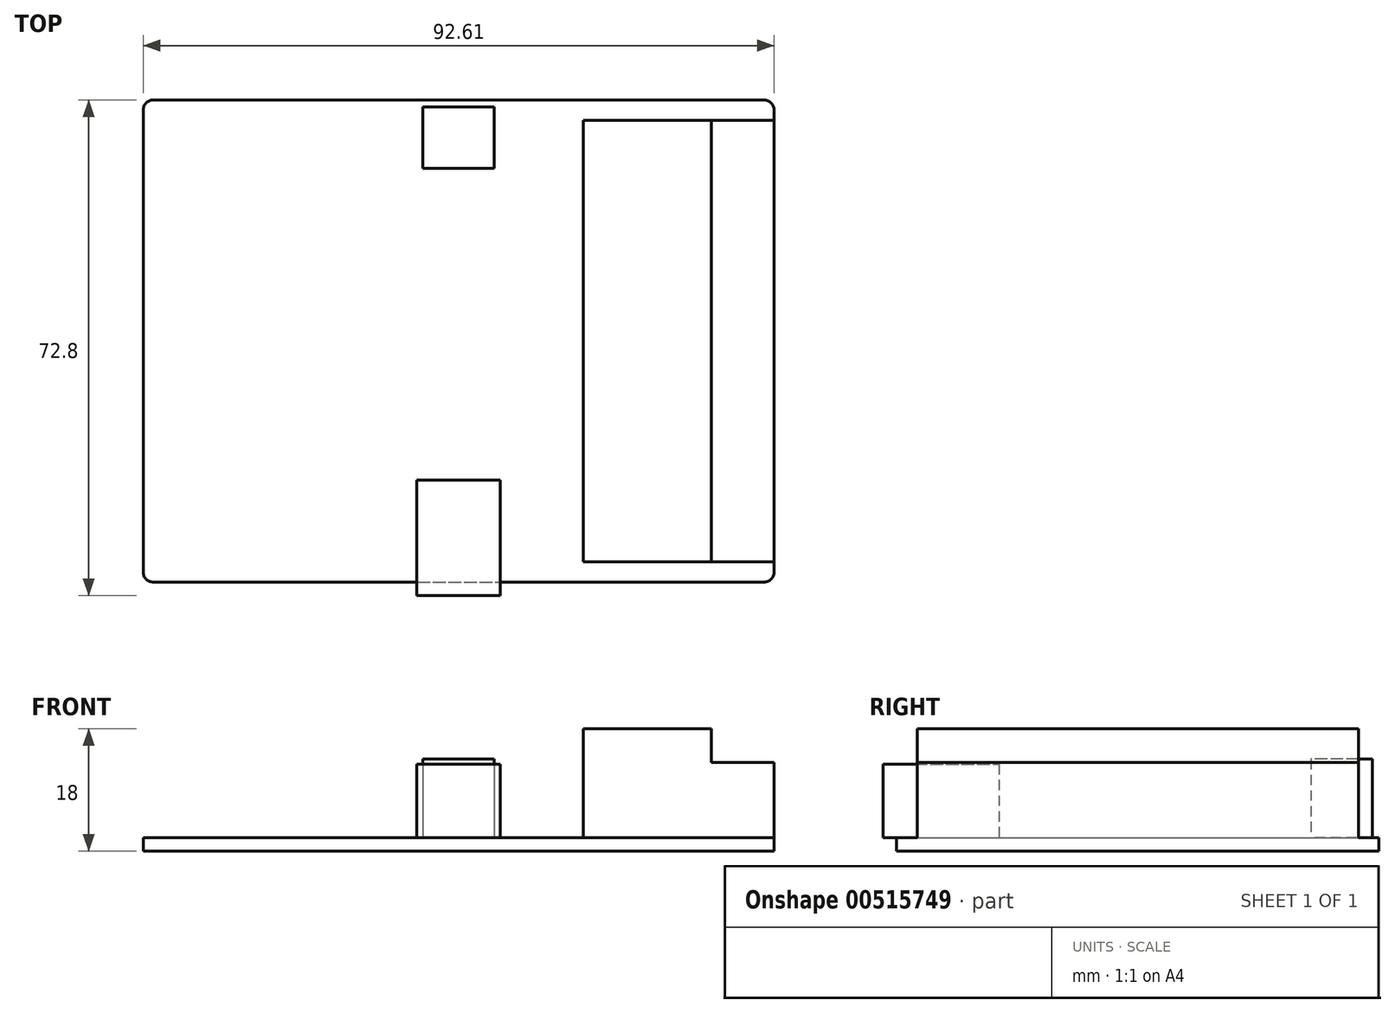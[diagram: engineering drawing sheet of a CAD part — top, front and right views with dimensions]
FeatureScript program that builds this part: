
annotation { "Feature Type Name" : "Feature", "Feature Type Description" : "" }
export const myFeature = defineFeature(function(context is Context, id is Id, definition is map)
    precondition{}
    {
        {
            var Q0;
            Q0=qCreatedBy(makeId("Top.planeOp"),FACE);
            var sketch = newSketch(context, id + "F0", { "sketchPlane" : qUnion([Q0])});
            skLineSegment(sketch, "E0.bottom", {"start": v(0, 0) * mm, "end": v(92.6, 0) * mm});
            skLineSegment(sketch, "E0.top", {"start": v(0, 70.8) * mm, "end": v(92.6, 70.8) * mm});
            skLineSegment(sketch, "E0.left", {"start": v(0, 0) * mm, "end": v(0, 70.8) * mm});
            skLineSegment(sketch, "E0.right", {"start": v(92.6, 0) * mm, "end": v(92.6, 70.8) * mm});
            skSolve(sketch);
        }
        {
            var Q0;
            Q0=makeQuery(id+"F0.imprint","IMPRINT",FACE,{"disambiguationData":[TD([[makeQuery(id+"F0.imprint","IMPRINT",EDGE,{"derivedFrom":sQuery(id+"F0.wireOp",EDGE,"E0.bottom")}),1.0]])]});
            extrude(context, id + "F1", {"entities" : qUnion([Q0]), "depth" : 2 * mm, "offsetDistance" : 25 * mm});
        }
        {
            var Q0;
            Q0=makeQuery(id+"F1.opExtrude","CAP_FACE",FACE,{"disambiguationData":[OSD([sQuery(id+"F0.wireOp",EDGE,"E0.bottom"),sQuery(id+"F0.wireOp",EDGE,"E0.top"),sQuery(id+"F0.wireOp",EDGE,"E0.left"),sQuery(id+"F0.wireOp",EDGE,"E0.right")])],"isStart":false});
            var sketch = newSketch(context, id + "F2", { "sketchPlane" : qUnion([Q0])});
            skLineSegment(sketch, "E1.bottom", {"start": v(64.6, 3) * mm, "end": v(92.6, 3) * mm});
            skLineSegment(sketch, "E1.top", {"start": v(64.6, 67.8) * mm, "end": v(92.6, 67.8) * mm});
            skLineSegment(sketch, "E1.left", {"start": v(64.6, 3) * mm, "end": v(64.6, 67.8) * mm});
            skLineSegment(sketch, "E1.right", {"start": v(92.6, 3) * mm, "end": v(92.6, 67.8) * mm});
            skSolve(sketch);
        }
        {
            var Q0;
            Q0=makeQuery(id+"F2.imprint","IMPRINT",FACE,{"disambiguationData":[TD([[makeQuery(id+"F2.imprint","IMPRINT",EDGE,{"derivedFrom":sQuery(id+"F2.wireOp",EDGE,"E1.bottom")}),1.0]])]});
            extrude(context, id + "F3", {"entities" : qUnion([Q0]), "operationType" : NewBodyOperationType.ADD, "depth" : 16 * mm, "offsetDistance" : 25 * mm});
        }
        {
            var Q0;
            Q0=makeQuery(id+"F3.opExtrude","CAP_FACE",FACE,{"disambiguationData":[OSD([sQuery(id+"F2.wireOp",EDGE,"E1.bottom"),sQuery(id+"F2.wireOp",EDGE,"E1.top"),sQuery(id+"F2.wireOp",EDGE,"E1.left"),sQuery(id+"F2.wireOp",EDGE,"E1.right")])],"isStart":false});
            var sketch = newSketch(context, id + "F4", { "sketchPlane" : qUnion([Q0])});
            skLineSegment(sketch, "E2.bottom", {"start": v(64.6, 3) * mm, "end": v(83.4, 3) * mm});
            skLineSegment(sketch, "E2.top", {"start": v(64.6, 67.8) * mm, "end": v(83.4, 67.8) * mm});
            skLineSegment(sketch, "E2.left", {"start": v(64.6, 3) * mm, "end": v(64.6, 67.8) * mm});
            skLineSegment(sketch, "E2.right", {"start": v(83.4, 3) * mm, "end": v(83.4, 67.8) * mm});
            skLineSegment(sketch, "E3.bottom", {"start": v(83.4, 3) * mm, "end": v(92.6, 3) * mm});
            skLineSegment(sketch, "E3.top", {"start": v(83.4, 67.8) * mm, "end": v(92.6, 67.8) * mm});
            skLineSegment(sketch, "E3.right", {"start": v(92.6, 3) * mm, "end": v(92.6, 67.8) * mm});
            skSolve(sketch);
        }
        {
            var Q0;
            Q0=makeQuery(id+"F4.imprint","IMPRINT",FACE,{"disambiguationData":[TD([[makeQuery(id+"F4.imprint","IMPRINT",EDGE,{"derivedFrom":sQuery(id+"F4.wireOp",EDGE,"E3.bottom")}),1.0]])]});
            extrude(context, id + "F5", {"entities" : qUnion([Q0]), "operationType" : NewBodyOperationType.REMOVE, "oppositeDirection" : true, "depth" : 5 * mm, "offsetDistance" : 25 * mm});
        }
        {
            var Q0;
            Q0=makeQuery(id+"F1.opExtrude","SWEPT_FACE",FACE,{"disambiguationData":[OSD([sQuery(id+"F0.wireOp",EDGE,"E0.left")])]});
            var Q1;
            Q1=makeQuery(id+"F3.boolean.opBoolean","MERGE",FACE,{"derivedFrom":[makeQuery(id+"F1.opExtrude","SWEPT_FACE",FACE,{"disambiguationData":[OSD([sQuery(id+"F0.wireOp",EDGE,"E0.right")])]}),makeQuery(id+"F3.opExtrude","SWEPT_FACE",FACE,{"disambiguationData":[OSD([sQuery(id+"F2.wireOp",EDGE,"E1.right")])]})]});
            cPlane(context, id + "F6", {"entities" : qUnion([Q0, Q1]), "cplaneType" : CPlaneType.MID_PLANE, "offset" : 25 * mm, "width" : 150 * mm, "height" : 150 * mm});
        }
        {
            var Q0;
            Q0=makeQuery(id+"F1.opExtrude","CAP_FACE",FACE,{"disambiguationData":[OSD([sQuery(id+"F0.wireOp",EDGE,"E0.bottom"),sQuery(id+"F0.wireOp",EDGE,"E0.top"),sQuery(id+"F0.wireOp",EDGE,"E0.left"),sQuery(id+"F0.wireOp",EDGE,"E0.right")])],"isStart":false});
            var sketch = newSketch(context, id + "F7", { "sketchPlane" : qUnion([Q0])});
            skLineSegment(sketch, "E4.bottom", {"start": v(40.18, 0) * mm, "end": v(52.43, 0) * mm});
            skLineSegment(sketch, "E4.top", {"start": v(40.18, 15) * mm, "end": v(52.43, 15) * mm});
            skLineSegment(sketch, "E4.left", {"start": v(40.18, 0) * mm, "end": v(40.18, 15) * mm});
            skLineSegment(sketch, "E4.right", {"start": v(52.43, 0) * mm, "end": v(52.43, 15) * mm});
            skPoint(sketch, "E5", {"position": v(46.3, 0) * mm});
            skSolve(sketch);
        }
        {
            var Q0;
            Q0=makeQuery(id+"F7.imprint","IMPRINT",FACE,{"disambiguationData":[TD([[makeQuery(id+"F7.imprint","IMPRINT",EDGE,{"derivedFrom":sQuery(id+"F7.wireOp",EDGE,"E4.bottom")}),1.0]])]});
            extrude(context, id + "F8", {"entities" : qUnion([Q0]), "operationType" : NewBodyOperationType.ADD, "depth" : 10.75 * mm, "offsetDistance" : 25 * mm});
        }
        {
            var Q0;
            Q0=makeQuery(id+"F1.opExtrude","SWEPT_EDGE",EDGE,{"disambiguationData":[OSD([sQuery(id+"F0.wireOp",EDGE,"E0.top"),sQuery(id+"F0.wireOp",EDGE,"E0.right")])]});
            var Q1;
            Q1=makeQuery(id+"F1.opExtrude","SWEPT_EDGE",EDGE,{"disambiguationData":[OSD([sQuery(id+"F0.wireOp",EDGE,"E0.top"),sQuery(id+"F0.wireOp",EDGE,"E0.left")])]});
            var Q2;
            Q2=makeQuery(id+"F1.opExtrude","SWEPT_EDGE",EDGE,{"disambiguationData":[OSD([sQuery(id+"F0.wireOp",EDGE,"E0.bottom"),sQuery(id+"F0.wireOp",EDGE,"E0.left")])]});
            var Q3;
            Q3=makeQuery(id+"F1.opExtrude","SWEPT_EDGE",EDGE,{"disambiguationData":[OSD([sQuery(id+"F0.wireOp",EDGE,"E0.bottom"),sQuery(id+"F0.wireOp",EDGE,"E0.right")])]});
            fillet(context, id + "F9", {"entities" : qUnion([Q0, Q1, Q2, Q3]), "radius" : 1.5 * mm, "tangentPropagation" : true, "allowEdgeOverflow" : false});
        }
        {
            var Q0;
            Q0=makeQuery(id+"F8.boolean.opBoolean","MERGE",FACE,{"derivedFrom":[makeQuery(id+"F1.opExtrude","SWEPT_FACE",FACE,{"disambiguationData":[OSD([sQuery(id+"F0.wireOp",EDGE,"E0.bottom")])]}),makeQuery(id+"F8.opExtrude","SWEPT_FACE",FACE,{"disambiguationData":[OSD([sQuery(id+"F7.wireOp",EDGE,"E4.bottom")])]})]});
            var sketch = newSketch(context, id + "F10", { "sketchPlane" : qUnion([Q0])});
            skLineSegment(sketch, "E6.bottom", {"start": v(40.18, 2) * mm, "end": v(52.43, 2) * mm});
            skLineSegment(sketch, "E6.top", {"start": v(40.18, 12.75) * mm, "end": v(52.43, 12.75) * mm});
            skLineSegment(sketch, "E6.left", {"start": v(40.18, 2) * mm, "end": v(40.18, 12.75) * mm});
            skLineSegment(sketch, "E6.right", {"start": v(52.43, 2) * mm, "end": v(52.43, 12.75) * mm});
            skSolve(sketch);
        }
        {
            var Q0;
            Q0=makeQuery(id+"F10.imprint","IMPRINT",FACE,{"disambiguationData":[TD([[makeQuery(id+"F10.imprint","IMPRINT",EDGE,{"derivedFrom":sQuery(id+"F10.wireOp",EDGE,"E6.bottom")}),1.0]])]});
            extrude(context, id + "F11", {"entities" : qUnion([Q0]), "operationType" : NewBodyOperationType.ADD, "depth" : 2 * mm, "offsetDistance" : 25 * mm});
        }
        {
            var Q0;
            Q0=makeQuery(id+"F1.opExtrude","CAP_FACE",FACE,{"disambiguationData":[OSD([sQuery(id+"F0.wireOp",EDGE,"E0.bottom"),sQuery(id+"F0.wireOp",EDGE,"E0.top"),sQuery(id+"F0.wireOp",EDGE,"E0.left"),sQuery(id+"F0.wireOp",EDGE,"E0.right")])],"isStart":false});
            var sketch = newSketch(context, id + "F12", { "sketchPlane" : qUnion([Q0])});
            skLineSegment(sketch, "E7.bottom", {"start": v(51.55, 69.8) * mm, "end": v(41.05, 69.8) * mm});
            skLineSegment(sketch, "E7.top", {"start": v(51.55, 60.8) * mm, "end": v(41.05, 60.8) * mm});
            skLineSegment(sketch, "E7.left", {"start": v(51.55, 69.8) * mm, "end": v(51.55, 60.8) * mm});
            skLineSegment(sketch, "E7.right", {"start": v(41.05, 69.8) * mm, "end": v(41.05, 60.8) * mm});
            skLineSegment(sketch, "E8", {"start": v(46.3, 69.8) * mm, "end": v(46.3, 70.8) * mm, "construction": true});
            skSolve(sketch);
        }
        {
            var Q0;
            Q0 = qSketchRegion(id + "F12", true);
            extrude(context, id + "F13", {"entities" : qUnion([Q0]), "operationType" : NewBodyOperationType.ADD, "depth" : 11.5 * mm, "offsetDistance" : 25 * mm});
        }
    });
